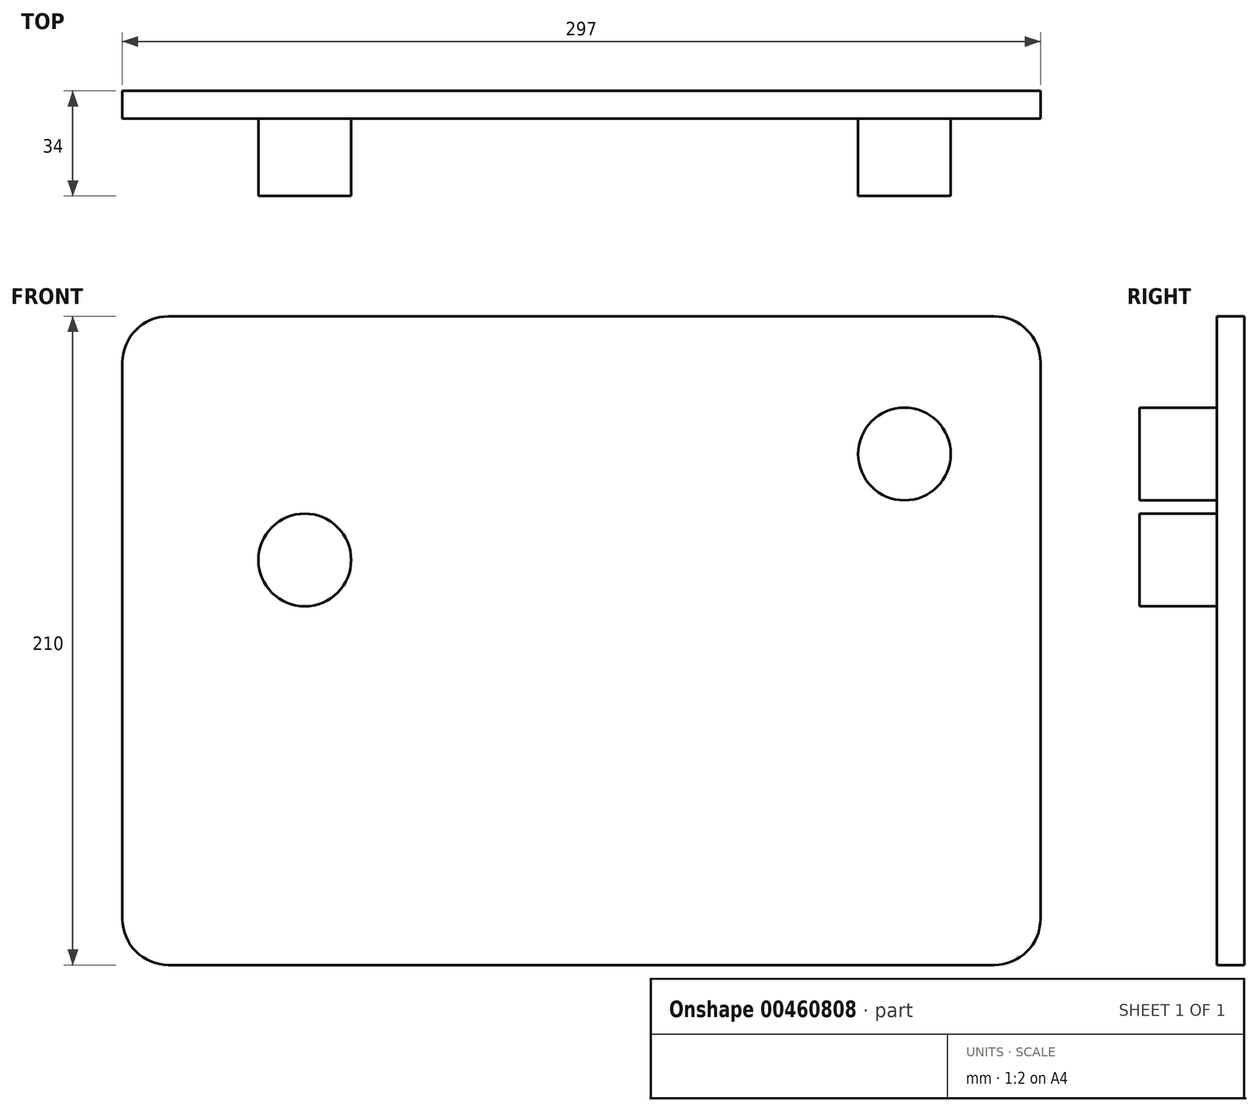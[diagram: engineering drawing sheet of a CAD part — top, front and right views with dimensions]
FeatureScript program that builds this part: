
annotation { "Feature Type Name" : "Feature", "Feature Type Description" : "" }
export const myFeature = defineFeature(function(context is Context, id is Id, definition is map)
    precondition{}
    {
        {
            var Q0;
            Q0=qCreatedBy(makeId("Front.planeOp"),FACE);
            var sketch = newSketch(context, id + "F0", { "sketchPlane" : qUnion([Q0])});
            skLineSegment(sketch, "E0.bottom", {"start": v(-137.36, 73.44) * mm, "end": v(129.64, 73.44) * mm});
            skLineSegment(sketch, "E0.top", {"start": v(-137.36, -136.56) * mm, "end": v(129.64, -136.56) * mm});
            skLineSegment(sketch, "E0.left", {"start": v(-152.36, 58.44) * mm, "end": v(-152.36, -121.56) * mm});
            skLineSegment(sketch, "E0.right", {"start": v(144.64, 58.44) * mm, "end": v(144.64, -121.56) * mm});
            skPoint(sketch, "E1.visualSharp", {"position": v(-152.36, 73.44) * mm});
            skArc(sketch, "E1.filletArc", {"start": v(-137.36, 73.44) * mm, "mid": v(-147.96, 69.04) * mm, "end": v(-152.36, 58.44) * mm});
            skPoint(sketch, "E2.visualSharp", {"position": v(144.64, 73.44) * mm});
            skArc(sketch, "E2.filletArc", {"start": v(144.64, 58.44) * mm, "mid": v(140.25, 69.04) * mm, "end": v(129.64, 73.44) * mm});
            skPoint(sketch, "E3.visualSharp", {"position": v(144.64, -136.56) * mm});
            skArc(sketch, "E3.filletArc", {"start": v(129.64, -136.56) * mm, "mid": v(140.25, -132.17) * mm, "end": v(144.64, -121.56) * mm});
            skPoint(sketch, "E4.visualSharp", {"position": v(-152.36, -136.56) * mm});
            skArc(sketch, "E4.filletArc", {"start": v(-152.36, -121.56) * mm, "mid": v(-147.96, -132.17) * mm, "end": v(-137.36, -136.56) * mm});
            skSolve(sketch);
        }
        {
            var Q0;
            Q0=makeQuery(id+"F0.imprint","IMPRINT",FACE,{"disambiguationData":[TD([[makeQuery(id+"F0.imprint","IMPRINT",EDGE,{"derivedFrom":sQuery(id+"F0.wireOp",EDGE,"E0.bottom")}),-1.0]])]});
            var Q1;
            Q1=sQuery(id+"F0.wireOp",EDGE,"E0.top");
            var Q2;
            Q2=sQuery(id+"F0.wireOp",EDGE,"E0.left");
            var Q3;
            Q3=sQuery(id+"F0.wireOp",EDGE,"E0.bottom");
            var Q4;
            Q4=sQuery(id+"F0.wireOp",EDGE,"E0.right");
            extrude(context, id + "F1", {"entities" : qUnion([Q0]), "surfaceEntities" : qUnion([Q1, Q2, Q3, Q4]), "depth" : 9 * mm});
        }
        {
            var Q0;
            Q0=makeQuery(id+"F1.opExtrude","CAP_FACE",FACE,{"disambiguationData":[OSD([sQuery(id+"F0.wireOp",EDGE,"E0.bottom"),sQuery(id+"F0.wireOp",EDGE,"E0.top"),sQuery(id+"F0.wireOp",EDGE,"E0.left"),sQuery(id+"F0.wireOp",EDGE,"E0.right")])],"isStart":false});
            var sketch = newSketch(context, id + "F2", { "sketchPlane" : qUnion([Q0])});
            skCircle(sketch, "E5", {"center": v(100.64, 28.87) * mm, "radius": 15 * mm});
            skCircle(sketch, "E6", {"center": v(-93.36, -5.43) * mm, "radius": 15 * mm});
            skText(sketch, "E7", { "text": "MR D IS OKAY", "fontName": "OpenSans-Regular.ttf"});
            const initialGuessF2  = {"E7": [-0.05672, -0.10874, 1, 0, 0.0452]};
            skSetInitialGuess(sketch, initialGuessF2);
            skSolve(sketch);
        }
        {
            var Q0;
            Q0=makeQuery(id+"F2.imprint","IMPRINT",FACE,{"disambiguationData":[TD([[makeQuery(id+"F2.imprint","IMPRINT",EDGE,{"derivedFrom":sQuery(id+"F2.wireOp",EDGE,"E6")}),1.0]])]});
            var Q1;
            Q1=makeQuery(id+"F2.imprint","IMPRINT",FACE,{"disambiguationData":[TD([[makeQuery(id+"F2.imprint","IMPRINT",EDGE,{"derivedFrom":sQuery(id+"F2.wireOp",EDGE,"E5")}),1.0]])]});
            extrude(context, id + "F3", {"entities" : qUnion([Q0, Q1]), "operationType" : NewBodyOperationType.ADD, "depth" : 25 * mm});
        }
    });
